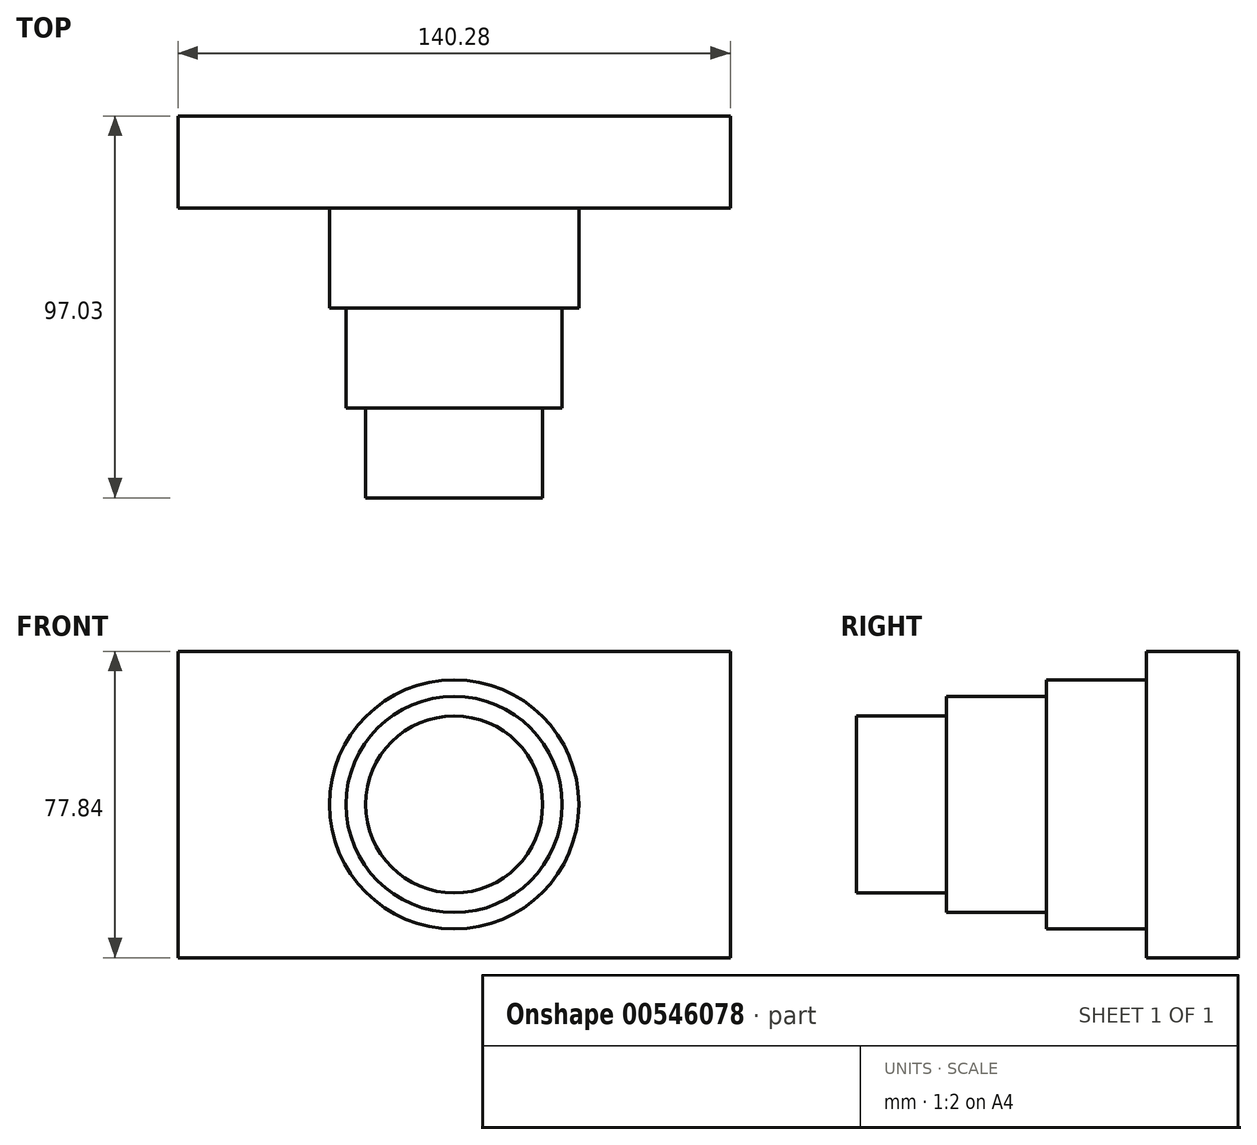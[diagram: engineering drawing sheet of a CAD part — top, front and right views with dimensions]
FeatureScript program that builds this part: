
annotation { "Feature Type Name" : "Feature", "Feature Type Description" : "" }
export const myFeature = defineFeature(function(context is Context, id is Id, definition is map)
    precondition{}
    {
        {
            var Q0;
            Q0=qCreatedBy(makeId("Front.planeOp"),FACE);
            var sketch = newSketch(context, id + "F0", { "sketchPlane" : qUnion([Q0])});
            skLineSegment(sketch, "E0.bottom", {"start": v(70.14, 38.92) * mm, "end": v(-70.14, 38.92) * mm});
            skLineSegment(sketch, "E0.top", {"start": v(70.14, -38.92) * mm, "end": v(-70.14, -38.92) * mm});
            skLineSegment(sketch, "E0.left", {"start": v(70.14, 38.92) * mm, "end": v(70.14, -38.92) * mm});
            skLineSegment(sketch, "E0.right", {"start": v(-70.14, 38.92) * mm, "end": v(-70.14, -38.92) * mm});
            skPoint(sketch, "E0.middle", {"position": v(0, 0) * mm});
            skSolve(sketch);
        }
        {
            var Q0;
            Q0 = qSketchRegion(id + "F0", true);
            extrude(context, id + "F1", {"entities" : qUnion([Q0]), "depth" : 23.37 * mm, "offsetDistance" : 25.4 * mm});
        }
        {
            var Q0;
            Q0=makeQuery(id+"F1.opExtrude","CAP_FACE",FACE,{"disambiguationData":[OSD([sQuery(id+"F0.wireOp",EDGE,"E0.bottom"),sQuery(id+"F0.wireOp",EDGE,"E0.top"),sQuery(id+"F0.wireOp",EDGE,"E0.left"),sQuery(id+"F0.wireOp",EDGE,"E0.right")])],"isStart":false});
            var sketch = newSketch(context, id + "F2", { "sketchPlane" : qUnion([Q0])});
            skCircle(sketch, "E1", {"center": v(0, 0) * mm, "radius": 31.67 * mm});
            skSolve(sketch);
        }
        {
            var Q0;
            Q0 = qSketchRegion(id + "F2", true);
            extrude(context, id + "F3", {"entities" : qUnion([Q0]), "operationType" : NewBodyOperationType.ADD, "depth" : 25.4 * mm, "offsetDistance" : 25.4 * mm});
        }
        {
            var Q0;
            Q0=makeQuery(id+"F3.opExtrude","CAP_FACE",FACE,{"disambiguationData":[OSD([sQuery(id+"F2.wireOp",EDGE,"E1")])],"isStart":false});
            var sketch = newSketch(context, id + "F4", { "sketchPlane" : qUnion([Q0])});
            skCircle(sketch, "E2", {"center": v(0, 0) * mm, "radius": 27.45 * mm});
            skSolve(sketch);
        }
        {
            var Q0;
            Q0 = qSketchRegion(id + "F4", true);
            extrude(context, id + "F5", {"entities" : qUnion([Q0]), "operationType" : NewBodyOperationType.ADD, "depth" : 25.4 * mm, "offsetDistance" : 25.4 * mm});
        }
        {
            var Q0;
            Q0=makeQuery(id+"F5.opExtrude","CAP_FACE",FACE,{"disambiguationData":[OSD([sQuery(id+"F4.wireOp",EDGE,"E2")])],"isStart":false});
            var sketch = newSketch(context, id + "F6", { "sketchPlane" : qUnion([Q0])});
            skCircle(sketch, "E3", {"center": v(0, 0) * mm, "radius": 22.5 * mm});
            skSolve(sketch);
        }
        {
            var Q0;
            Q0 = qSketchRegion(id + "F6", true);
            extrude(context, id + "F7", {"entities" : qUnion([Q0]), "operationType" : NewBodyOperationType.ADD, "depth" : 22.86 * mm, "offsetDistance" : 25.4 * mm});
        }
    });
